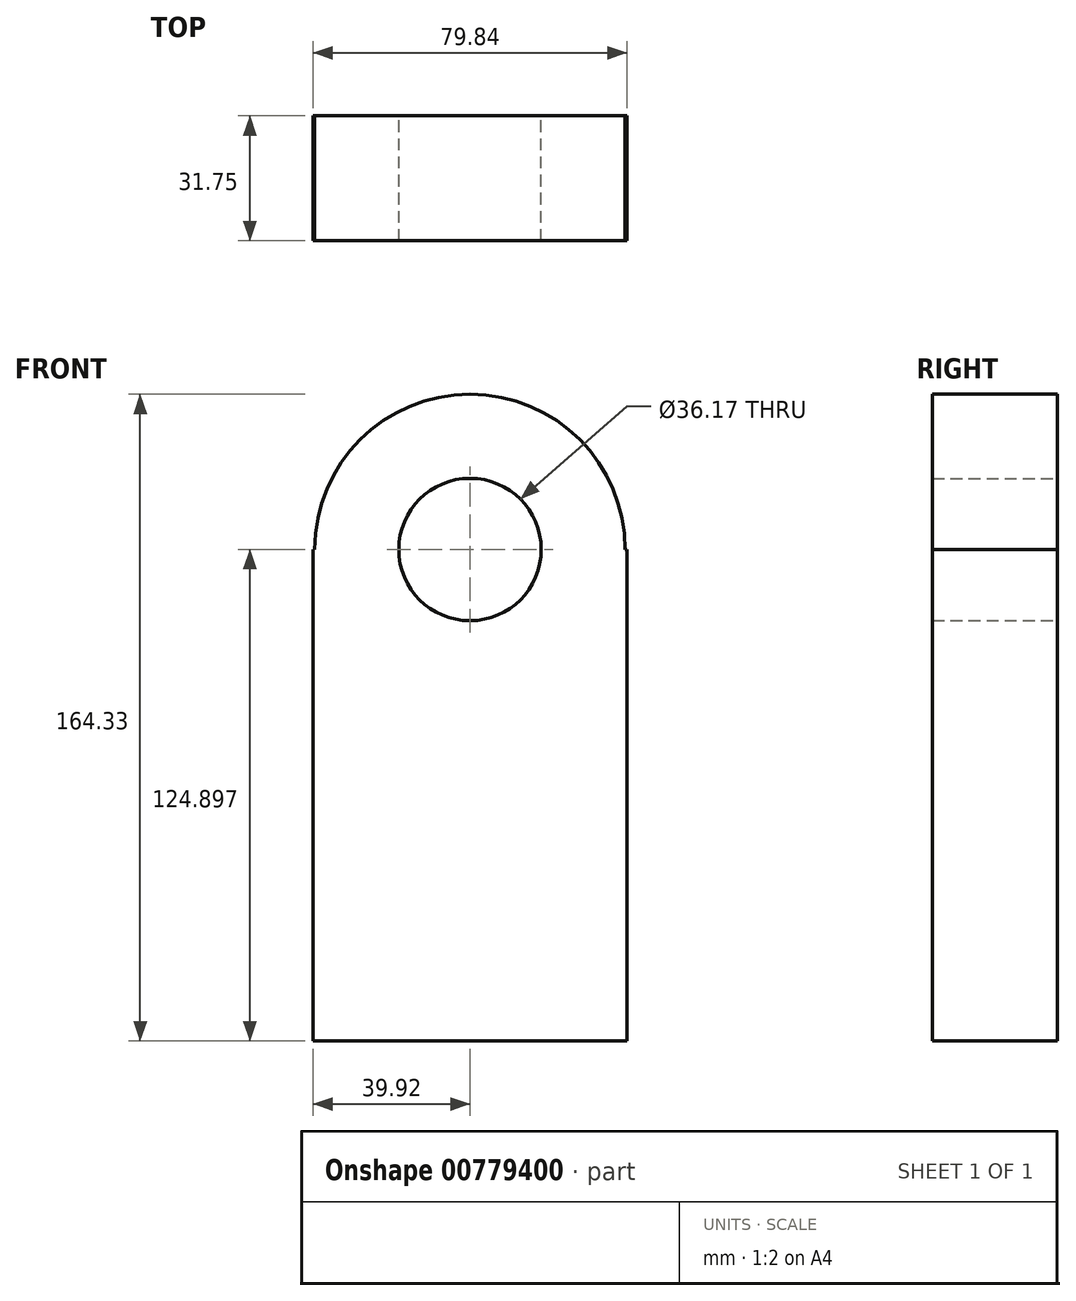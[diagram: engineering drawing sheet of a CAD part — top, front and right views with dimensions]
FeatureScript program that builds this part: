
annotation { "Feature Type Name" : "Feature", "Feature Type Description" : "" }
export const myFeature = defineFeature(function(context is Context, id is Id, definition is map)
    precondition{}
    {
        {
            var Q0;
            Q0=qCreatedBy(makeId("Front.planeOp"),FACE);
            var sketch = newSketch(context, id + "F0", { "sketchPlane" : qUnion([Q0])});
            skLineSegment(sketch, "E0.bottom", {"start": v(-39.92, 62.45) * mm, "end": v(-39.44, 62.45) * mm});
            skLineSegment(sketch, "E0.top", {"start": v(-39.92, -62.45) * mm, "end": v(39.92, -62.45) * mm});
            skLineSegment(sketch, "E0.left", {"start": v(-39.92, 62.45) * mm, "end": v(-39.92, -62.45) * mm});
            skLineSegment(sketch, "E0.right", {"start": v(39.92, 62.45) * mm, "end": v(39.92, -62.45) * mm});
            skPoint(sketch, "E0.middle", {"position": v(0, 0) * mm});
            skArc(sketch, "E1", {"start": v(39.44, 62.45) * mm, "mid": v(0, 101.88) * mm, "end": v(-39.44, 62.45) * mm});
            skCircle(sketch, "E2", {"center": v(0, 62.45) * mm, "radius": 18.09 * mm});
            skLineSegment(sketch, "E3.trimOffspring", {"start": v(-18.09, 62.45) * mm, "end": v(18.09, 62.45) * mm});
            skLineSegment(sketch, "E4.trimOffspring", {"start": v(39.44, 62.45) * mm, "end": v(39.92, 62.45) * mm});
            skSolve(sketch);
        }
        {
            var Q0;
            Q0=makeQuery(id+"F0.imprint","IMPRINT",FACE,{"disambiguationData":[TD([[makeQuery(id+"F0.imprint","IMPRINT",EDGE,{"derivedFrom":sQuery(id+"F0.wireOp",EDGE,"E0.bottom")}),-1.0]])]});
            extrude(context, id + "F1", {"entities" : qUnion([Q0]), "depth" : 31.75 * mm, "offsetDistance" : 25.4 * mm});
        }
    });
